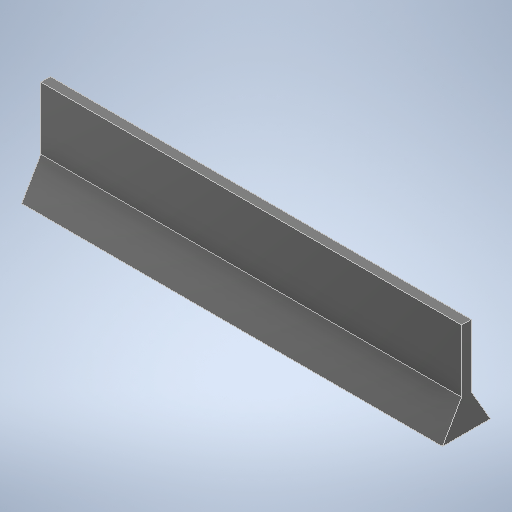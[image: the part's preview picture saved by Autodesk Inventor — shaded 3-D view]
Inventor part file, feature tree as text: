
AUTODESK INVENTOR PART (.ipt)
format: ipt  version: 2025.1 (Build 291241020, 241B)  size: 582,144 bytes
history: native  units: mm
features: sketch x3, extrude x2, projected_geometry x2, hole x1
ambient origin geometry x8: Origin, YZ Plane, XZ Plane, XY Plane, X Axis, Y Axis, Z Axis, Center Point
bodies: Solid1 (feature_tree)
feature tree (8):
  extrude  "Extrusion1"  Depth=50.0mm
  hole  "Hole1"  [1 undecoded]
  extrude  "Extrusion2"  Depth=5.0mm
  sketch  "Sketch1"  dims[d0=220.0mm d1=50.0mm]
  sketch  "Sketch2"  dims[d2=5.0mm d3=0.0mm d4=5.0mm]
  sketch  "Sketch3"  dims[d5=220.0mm d6=2.5mm d7=38.0mm d8=48.0mm d9=48.0mm d10=48.0mm d11=4.8mm d12=6.0mm d13=4.0mm d14=2.0mm d15=90.0deg d16=10.0mm d17=0.0mm d18=10.0mm d19=60.0deg d20=5.0mm d21=0.0mm d22=0.5mm d23=0.872665mm]
  projected_geometry  "Projected Loop1"
  projected_geometry  "Projected Loop2"
note: 1 required parameter value undecoded (feature->parameter linkage not recoverable at this tier; creation-order binding heuristic only, values carry confidence <= 0.55)
